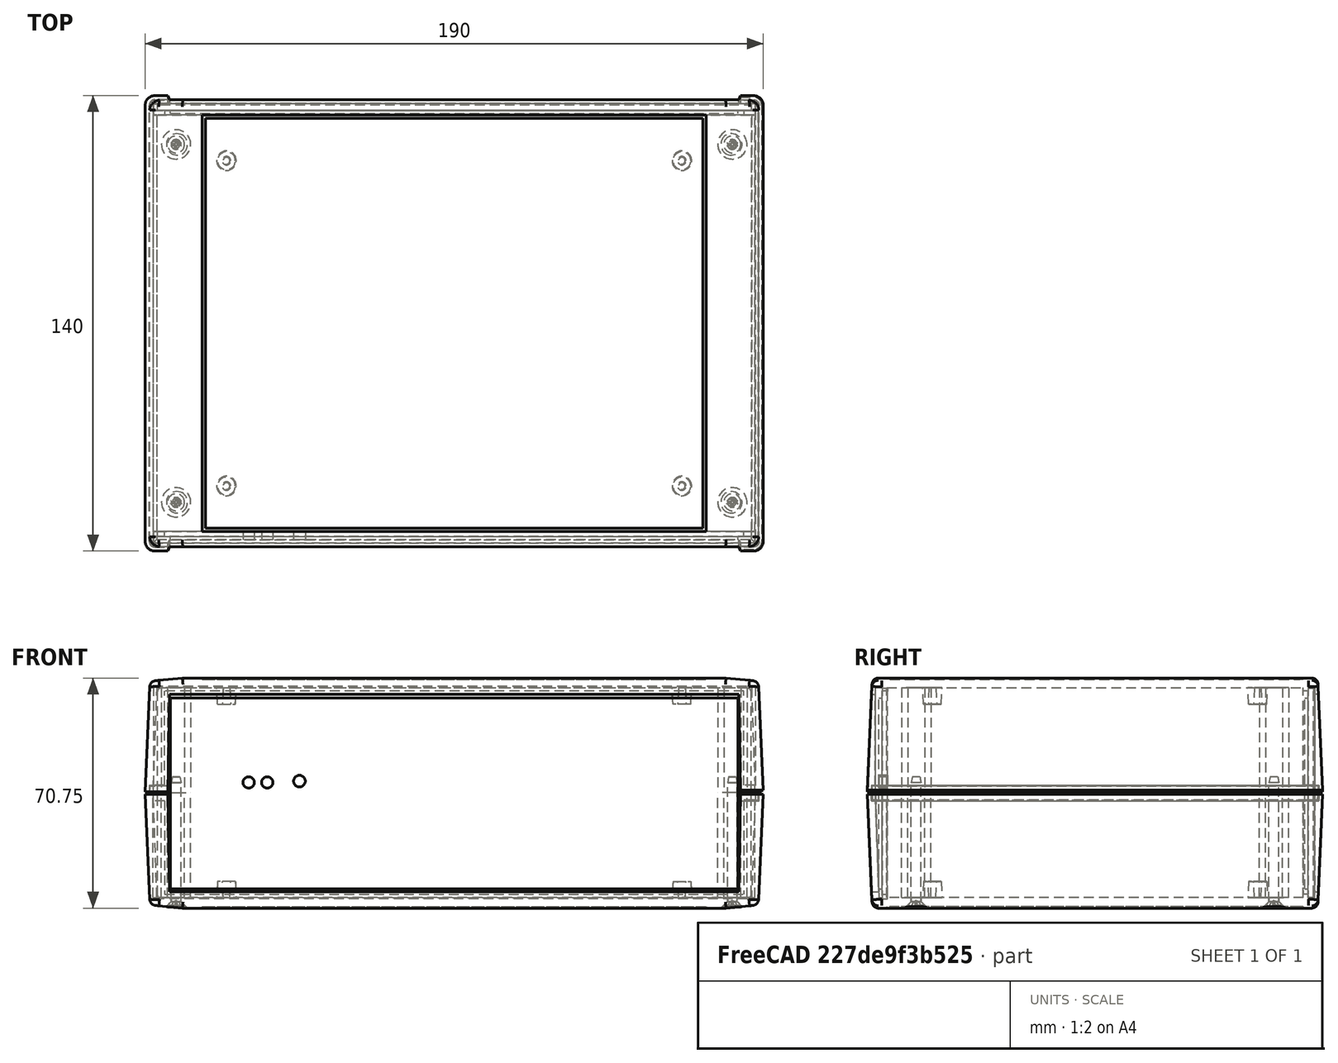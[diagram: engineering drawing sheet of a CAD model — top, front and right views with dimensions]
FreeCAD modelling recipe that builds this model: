
FCSTD DOCUMENT  (FreeCAD 0.17R13541 (Git))
Label: BBSensor
License: All rights reserved
LicenseURL: http://en.wikipedia.org/wiki/All_rights_reserved
objects: Part::Feature×8, Part::Cylinder×3, App::Part×1, App::VRMLObject×1
note: 11 computed .brp shape members not serialized (recipe doc carries the construction recipe); baked Part::Feature solids carry a one-line shape summary decoded from their .brp

FEATURE [Part::Feature] Part__Feature  label="2051Lb-01A"
  shape: bbox 190 x 140 x 37.62 mm, 129 faces (baked)
FEATURE [Part::Feature] Part__Feature001  label="2051LT-01_0A"
  Placement = pos=(0,0,0.75) rot=(0,0,1;0rad)
  shape: bbox 190 x 140 x 37.63 mm, 121 faces (baked)
FEATURE [Part::Feature] Part__Feature002  label="2051L-p01A"
  Placement = pos=(0,0,0.75) rot=(0,1,0;3.14159rad)
  shape: bbox 182.5 x 2.7 x 64.7 mm, 15 faces (baked)
FEATURE [Part::Feature] Part__Feature003  label="2051L-p01A001"
  Placement = pos=(0,-131,0.75) rot=(0,1,0;3.14159rad)
  shape: bbox 182.5 x 2.7 x 64.7 mm, 15 faces (baked)
FEATURE [Part::Feature] Part__Feature005  label="Cross Recessed Flat Countersunk Head Tapping Screw - Type F - Type I - Metric M3x0.5 x 16"
  Placement = pos=(85.5,55,-34.38) rot=(0,-1,0;1.5708rad)
  shape: bbox 5.2 x 5.2 x 40 mm, 27 faces (baked)
FEATURE [Part::Feature] Part__Feature006  label="Cross Recessed Flat Countersunk Head Tapping Screw - Type F - Type I - Metric M3x0.5 x 017"
  Placement = pos=(85.5,-55,-34.38) rot=(0,-1,0;1.5708rad)
  shape: bbox 5.2 x 5.2 x 40 mm, 27 faces (baked)
FEATURE [Part::Feature] Part__Feature007  label="Cross Recessed Flat Countersunk Head Tapping Screw - Type F - Type I - Metric M3x0.5 x 018"
  Placement = pos=(-85.5,-55,-34.38) rot=(0,-1,0;1.5708rad)
  shape: bbox 5.2 x 5.2 x 40 mm, 27 faces (baked)
FEATURE [Part::Feature] Part__Feature008  label="Cross Recessed Flat Countersunk Head Tapping Screw - Type F - Type I - Metric M3x0.5 x 019"
  Placement = pos=(-85.5,55,-34.38) rot=(0,-1,0;1.5708rad)
  shape: bbox 5.2 x 5.2 x 40 mm, 27 faces (baked)
FEATURE [App::Part] RM2055L___SCREWS  label="RM2055L"
  Group = -> [Part__Feature,Part__Feature001,Part__Feature002,Part__Feature003,Part__Feature005,Part__Feature006,Part__Feature007,Part__Feature008]
  License = CC BY 3.0
  LicenseURL = http://creativecommons.org/licenses/by/3.0/
  Origin = -> Origin
FEATURE [App::VRMLObject] BBSensor
  Placement = pos=(-23.5,-67,0) rot=(0,0,1;0rad)
FEATURE [Part::Cylinder] Cylinder001
  Angle = 360
  AttacherType = Attacher::AttachEngine3D
  Height = 2.7
  Placement = pos=(-47.575,-63.8,4.28) rot=(1,0,0;1.5708rad)
  Radius = 1.8
FEATURE [Part::Cylinder] Cylinder002
  Angle = 360
  AttacherType = Attacher::AttachEngine3D
  Height = 2.7
  Placement = pos=(-63.175,-63.8,3.9) rot=(1,0,0;1.5708rad)
  Radius = 1.75
FEATURE [Part::Cylinder] Cylinder003
  Angle = 360
  AttacherType = Attacher::AttachEngine3D
  Height = 2.7
  Placement = pos=(-57.47,-63.8,3.9) rot=(1,0,0;1.5708rad)
  Radius = 1.75
